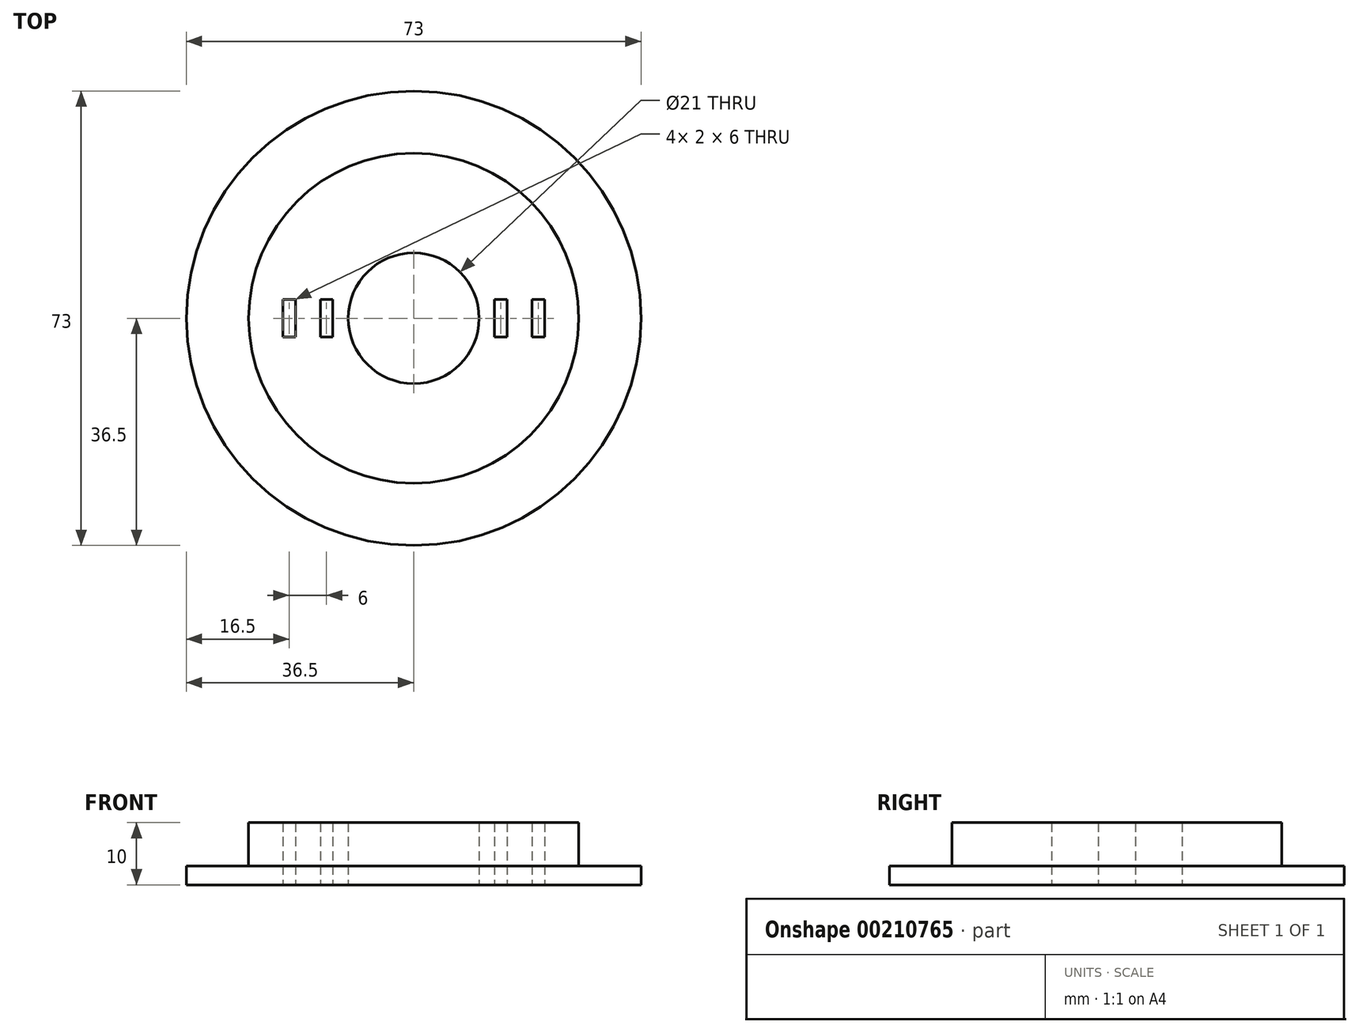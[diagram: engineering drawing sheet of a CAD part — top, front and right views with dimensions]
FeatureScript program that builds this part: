
annotation { "Feature Type Name" : "Feature", "Feature Type Description" : "" }
export const myFeature = defineFeature(function(context is Context, id is Id, definition is map)
    precondition{}
    {
        {
            var Q0;
            Q0=qCreatedBy(makeId("Top.planeOp"),FACE);
            var sketch = newSketch(context, id + "F0", { "sketchPlane" : qUnion([Q0])});
            skCircle(sketch, "E0", {"center": v(0, 0) * mm, "radius": 26.5 * mm});
            skCircle(sketch, "E1.0", {"center": v(0, 0) * mm, "radius": 36.5 * mm});
            skCircle(sketch, "E2", {"center": v(0, 0) * mm, "radius": 10.5 * mm});
            skSolve(sketch);
        }
        {
            var Q0;
            Q0=makeQuery(id+"F0.imprint","IMPRINT",FACE,{"disambiguationData":[TD([[makeQuery(id+"F0.imprint","IMPRINT",EDGE,{"derivedFrom":sQuery(id+"F0.wireOp",EDGE,"E0")}),-1.0]])]});
            extrude(context, id + "F1", {"entities" : qUnion([Q0]), "depth" : 3 * mm});
        }
        {
            var Q0;
            Q0=makeQuery(id+"F0.imprint","IMPRINT",FACE,{"disambiguationData":[TD([[makeQuery(id+"F0.imprint","IMPRINT",EDGE,{"derivedFrom":sQuery(id+"F0.wireOp",EDGE,"E0")}),1.0]])]});
            extrude(context, id + "F2", {"entities" : qUnion([Q0]), "operationType" : NewBodyOperationType.ADD, "depth" : 10 * mm});
        }
        {
            var Q0;
            Q0=qCreatedBy(makeId("Top.planeOp"),FACE);
            var sketch = newSketch(context, id + "F3", { "sketchPlane" : qUnion([Q0])});
            skLineSegment(sketch, "E3", {"start": v(-40.55, 0) * mm, "end": v(41.23, 0) * mm, "construction": true});
            skLineSegment(sketch, "E4.bottom", {"start": v(-19, 3) * mm, "end": v(-21, 3) * mm});
            skLineSegment(sketch, "E4.top", {"start": v(-19, -3) * mm, "end": v(-21, -3) * mm});
            skLineSegment(sketch, "E4.left", {"start": v(-19, 3) * mm, "end": v(-19, -3) * mm});
            skLineSegment(sketch, "E4.right", {"start": v(-21, 3) * mm, "end": v(-21, -3) * mm});
            skPoint(sketch, "E4.middle", {"position": v(-20, 0) * mm});
            skLineSegment(sketch, "E5.bottom", {"start": v(-13, 3) * mm, "end": v(-15, 3) * mm});
            skLineSegment(sketch, "E5.top", {"start": v(-13, -3) * mm, "end": v(-15, -3) * mm});
            skLineSegment(sketch, "E5.left", {"start": v(-13, 3) * mm, "end": v(-13, -3) * mm});
            skLineSegment(sketch, "E5.right", {"start": v(-15, 3) * mm, "end": v(-15, -3) * mm});
            skPoint(sketch, "E5.middle", {"position": v(-14, 0) * mm});
            skLineSegment(sketch, "E6.MirrorCS", {"start": v(19, 3) * mm, "end": v(21, 3) * mm});
            skLineSegment(sketch, "E7.MirrorCS", {"start": v(19, -3) * mm, "end": v(21, -3) * mm});
            skLineSegment(sketch, "E8.MirrorCS", {"start": v(19, 3) * mm, "end": v(19, -3) * mm});
            skLineSegment(sketch, "E9.MirrorCS", {"start": v(21, 3) * mm, "end": v(21, -3) * mm});
            skLineSegment(sketch, "E10.MirrorCS", {"start": v(15, 3) * mm, "end": v(15, -3) * mm});
            skLineSegment(sketch, "E11.MirrorCS", {"start": v(13, 3) * mm, "end": v(13, -3) * mm});
            skLineSegment(sketch, "E12.MirrorCS", {"start": v(13, 3) * mm, "end": v(15, 3) * mm});
            skLineSegment(sketch, "E13.MirrorCS", {"start": v(13, -3) * mm, "end": v(15, -3) * mm});
            skPoint(sketch, "E14.MirrorP", {"position": v(14, 0) * mm});
            skPoint(sketch, "E15.MirrorP", {"position": v(20, 0) * mm});
            skSolve(sketch);
        }
        {
            var Q0;
            Q0 = qSketchRegion(id + "F3", true);
            extrude(context, id + "F4", {"entities" : qUnion([Q0]), "operationType" : NewBodyOperationType.REMOVE, "depth" : 25 * mm});
        }
    });
